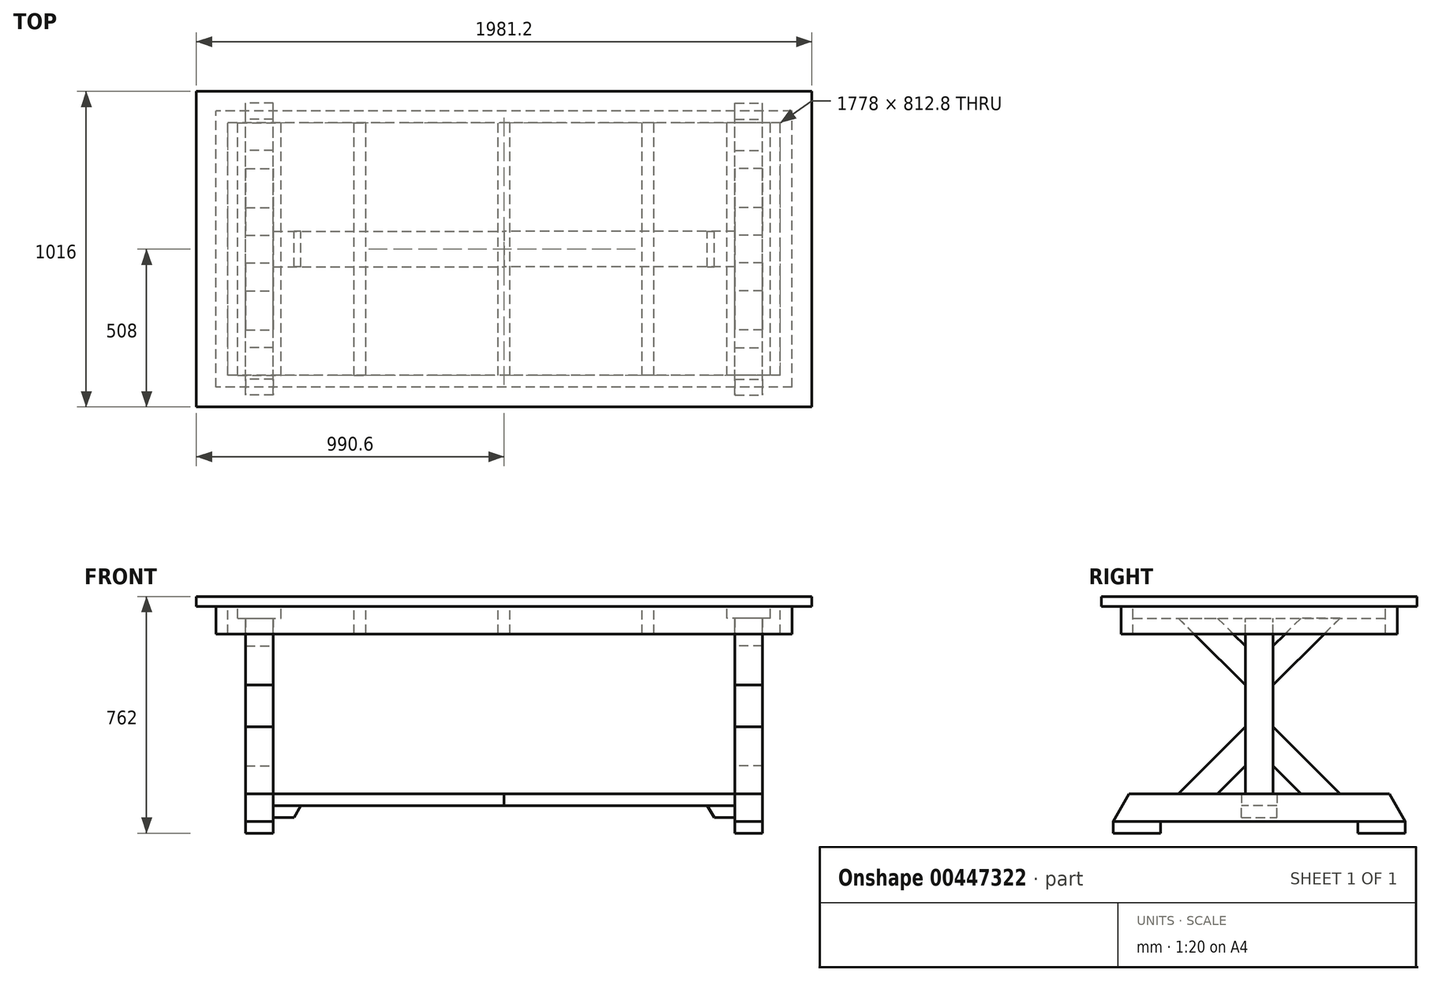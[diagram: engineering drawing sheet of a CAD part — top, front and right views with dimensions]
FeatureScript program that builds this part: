
annotation { "Feature Type Name" : "Feature", "Feature Type Description" : "" }
export const myFeature = defineFeature(function(context is Context, id is Id, definition is map)
    precondition{}
    {
        {
            var Q0;
            Q0=qCreatedBy(makeId("Top.planeOp"),FACE);
            var sketch = newSketch(context, id + "F0", { "sketchPlane" : qUnion([Q0])});
            skLineSegment(sketch, "E0.bottom", {"start": v(990.6, 508) * mm, "end": v(-990.6, 508) * mm});
            skLineSegment(sketch, "E0.top", {"start": v(990.6, -508) * mm, "end": v(-990.6, -508) * mm});
            skLineSegment(sketch, "E0.left", {"start": v(990.6, 508) * mm, "end": v(990.6, -508) * mm});
            skLineSegment(sketch, "E0.right", {"start": v(-990.6, 508) * mm, "end": v(-990.6, -508) * mm});
            skPoint(sketch, "E0.middle", {"position": v(0, 0) * mm});
            skSolve(sketch);
        }
        {
            var Q0;
            Q0 = qSketchRegion(id + "F0", true);
            extrude(context, id + "F1", {"entities" : qUnion([Q0]), "depth" : 31.75 * mm});
        }
        {
            var Q0;
            Q0=makeQuery(id+"F1.opExtrude","CAP_FACE",FACE,{"disambiguationData":[OSD([sQuery(id+"F0.wireOp",EDGE,"E0.bottom"),sQuery(id+"F0.wireOp",EDGE,"E0.top"),sQuery(id+"F0.wireOp",EDGE,"E0.left"),sQuery(id+"F0.wireOp",EDGE,"E0.right")])],"isStart":true});
            var sketch = newSketch(context, id + "F2", { "sketchPlane" : qUnion([Q0])});
            skLineSegment(sketch, "E1.bottom", {"start": v(889, 406.4) * mm, "end": v(-889, 406.4) * mm});
            skLineSegment(sketch, "E1.top", {"start": v(889, -406.4) * mm, "end": v(-889, -406.4) * mm});
            skLineSegment(sketch, "E1.left", {"start": v(889, 406.4) * mm, "end": v(889, -406.4) * mm});
            skLineSegment(sketch, "E1.right", {"start": v(-889, 406.4) * mm, "end": v(-889, -406.4) * mm});
            skPoint(sketch, "E1.middle", {"position": v(0, 0) * mm});
            skLineSegment(sketch, "E2.0", {"start": v(927.1, 444.5) * mm, "end": v(-927.1, 444.5) * mm});
            skLineSegment(sketch, "E2.1", {"start": v(927.1, 444.5) * mm, "end": v(927.1, -444.5) * mm});
            skLineSegment(sketch, "E2.2", {"start": v(927.1, -444.5) * mm, "end": v(-927.1, -444.5) * mm});
            skLineSegment(sketch, "E2.3", {"start": v(-927.1, 444.5) * mm, "end": v(-927.1, -444.5) * mm});
            skLineSegment(sketch, "E3", {"start": v(0, 508) * mm, "end": v(0, 444.5) * mm, "construction": true});
            skLineSegment(sketch, "E4", {"start": v(-927.1, 0) * mm, "end": v(-990.6, 0) * mm, "construction": true});
            skSolve(sketch);
        }
        {
            var Q0;
            Q0 = qSketchRegion(id + "F2", true);
            extrude(context, id + "F3", {"entities" : qUnion([Q0]), "depth" : 88.9 * mm});
        }
        {
            var Q0;
            Q0=makeQuery(id+"F1.opExtrude","CAP_FACE",FACE,{"disambiguationData":[OSD([sQuery(id+"F0.wireOp",EDGE,"E0.bottom"),sQuery(id+"F0.wireOp",EDGE,"E0.top"),sQuery(id+"F0.wireOp",EDGE,"E0.left"),sQuery(id+"F0.wireOp",EDGE,"E0.right")])],"isStart":true});
            var sketch = newSketch(context, id + "F4", { "sketchPlane" : qUnion([Q0])});
            skLineSegment(sketch, "E5.bottom", {"start": v(-857.25, 406.4) * mm, "end": v(-717.55, 406.4) * mm});
            skLineSegment(sketch, "E5.top", {"start": v(-857.25, -406.4) * mm, "end": v(-717.55, -406.4) * mm});
            skLineSegment(sketch, "E5.left", {"start": v(-857.25, 406.4) * mm, "end": v(-857.25, -406.4) * mm});
            skLineSegment(sketch, "E5.right", {"start": v(-717.55, 406.4) * mm, "end": v(-717.55, -406.4) * mm});
            skLineSegment(sketch, "E6", {"start": v(-787.4, 406.4) * mm, "end": v(-787.4, -406.4) * mm, "construction": true});
            skLineSegment(sketch, "E7", {"start": v(0, 0) * mm, "end": v(0, 564.1) * mm, "construction": true});
            skPoint(sketch, "E7.endSnap0", {"position": v(0, 508) * mm});
            skSolve(sketch);
        }
        {
            var Q0;
            Q0 = qSketchRegion(id + "F4", true);
            extrude(context, id + "F5", {"entities" : qUnion([Q0]), "depth" : 38.1 * mm});
        }
        {
            var Q0;
            Q0=makeQuery(id+"F5.opExtrude","CAP_FACE",FACE,{"disambiguationData":[OSD([sQuery(id+"F4.wireOp",EDGE,"E5.bottom"),sQuery(id+"F4.wireOp",EDGE,"E5.top"),sQuery(id+"F4.wireOp",EDGE,"E5.left"),sQuery(id+"F4.wireOp",EDGE,"E5.right")])],"isStart":false});
            var sketch = newSketch(context, id + "F6", { "sketchPlane" : qUnion([Q0])});
            skLineSegment(sketch, "E8.bottom", {"start": v(-831.85, 44.45) * mm, "end": v(-742.95, 44.45) * mm});
            skLineSegment(sketch, "E8.top", {"start": v(-831.85, -44.45) * mm, "end": v(-742.95, -44.45) * mm});
            skLineSegment(sketch, "E8.left", {"start": v(-831.85, 44.45) * mm, "end": v(-831.85, -44.45) * mm});
            skLineSegment(sketch, "E8.right", {"start": v(-742.95, 44.45) * mm, "end": v(-742.95, -44.45) * mm});
            skPoint(sketch, "E9.orphan", {"position": v(-717.55, -44.45) * mm});
            skLineSegment(sketch, "E10", {"start": v(-787.4, 44.45) * mm, "end": v(-787.4, 0) * mm, "construction": true});
            skLineSegment(sketch, "E11", {"start": v(-787.4, 0) * mm, "end": v(-717.55, 0) * mm, "construction": true});
            skSolve(sketch);
        }
        {
            var Q0;
            Q0 = qSketchRegion(id + "F6", true);
            extrude(context, id + "F7", {"entities" : qUnion([Q0]), "depth" : 565.15 * mm});
        }
        {
            var Q0;
            Q0=makeQuery(id+"F7.opExtrude","SWEPT_FACE",FACE,{"disambiguationData":[OSD([sQuery(id+"F6.wireOp",EDGE,"E8.right")])]});
            var sketch = newSketch(context, id + "F8", { "sketchPlane" : qUnion([Q0])});
            skLineSegment(sketch, "E12", {"start": v(-134.25, -38.1) * mm, "end": v(-44.45, -127.9) * mm});
            skLineSegment(sketch, "E13", {"start": v(-44.45, -127.9) * mm, "end": v(-44.45, -320.68) * mm});
            skLineSegment(sketch, "E14", {"start": v(-44.45, -253.63) * mm, "end": v(-259.98, -38.1) * mm});
            skLineSegment(sketch, "E15", {"start": v(-259.98, -38.1) * mm, "end": v(-134.25, -38.1) * mm});
            skLineSegment(sketch, "E16", {"start": v(0, 0) * mm, "end": v(0, -702.78) * mm, "construction": true});
            skLineSegment(sketch, "E17.MirrorCS", {"start": v(134.25, -38.1) * mm, "end": v(44.45, -127.9) * mm});
            skLineSegment(sketch, "E18.MirrorCS", {"start": v(44.45, -127.9) * mm, "end": v(44.45, -320.68) * mm});
            skLineSegment(sketch, "E19.MirrorCS", {"start": v(44.45, -253.63) * mm, "end": v(259.98, -38.1) * mm});
            skLineSegment(sketch, "E20.MirrorCS", {"start": v(259.98, -38.1) * mm, "end": v(134.25, -38.1) * mm});
            skLineSegment(sketch, "E21", {"start": v(44.45, -320.68) * mm, "end": v(-44.45, -320.68) * mm, "construction": true});
            skLineSegment(sketch, "E22.MirrorCS", {"start": v(44.45, -513.45) * mm, "end": v(44.45, -320.68) * mm});
            skLineSegment(sketch, "E23.MirrorCS", {"start": v(134.25, -603.25) * mm, "end": v(44.45, -513.45) * mm});
            skLineSegment(sketch, "E24.MirrorCS", {"start": v(44.45, -387.72) * mm, "end": v(259.98, -603.25) * mm});
            skLineSegment(sketch, "E25.MirrorCS", {"start": v(259.98, -603.25) * mm, "end": v(134.25, -603.25) * mm});
            skLineSegment(sketch, "E26.MirrorCS", {"start": v(-134.25, -603.25) * mm, "end": v(-44.45, -513.45) * mm});
            skLineSegment(sketch, "E27.MirrorCS", {"start": v(-259.98, -603.25) * mm, "end": v(-134.25, -603.25) * mm});
            skLineSegment(sketch, "E28.MirrorCS", {"start": v(-44.45, -387.72) * mm, "end": v(-259.98, -603.25) * mm});
            skLineSegment(sketch, "E29.MirrorCS", {"start": v(-44.45, -513.45) * mm, "end": v(-44.45, -320.68) * mm});
            skSolve(sketch);
        }
        {
            var Q0;
            Q0 = qSketchRegion(id + "F8", true);
            extrude(context, id + "F9", {"entities" : qUnion([Q0]), "oppositeDirection" : true, "depth" : 88.9 * mm});
        }
        {
            var Q0;
            Q0=makeQuery(id+"F7.opExtrude","SWEPT_FACE",FACE,{"disambiguationData":[OSD([sQuery(id+"F6.wireOp",EDGE,"E8.left")])]});
            var sketch = newSketch(context, id + "F10", { "sketchPlane" : qUnion([Q0])});
            skLineSegment(sketch, "E30.bottom", {"start": v(418.57, -603.25) * mm, "end": v(-418.57, -603.25) * mm});
            skLineSegment(sketch, "E30.top", {"start": v(469.9, -692.15) * mm, "end": v(-469.9, -692.15) * mm});
            skPoint(sketch, "E30.middle", {"position": v(0, -647.7) * mm});
            skLineSegment(sketch, "E31", {"start": v(0, 0) * mm, "end": v(0, -647.7) * mm, "construction": true});
            skLineSegment(sketch, "E32", {"start": v(-418.57, -603.25) * mm, "end": v(-469.9, -692.15) * mm});
            skLineSegment(sketch, "E33.MirrorCS", {"start": v(418.57, -603.25) * mm, "end": v(469.9, -692.15) * mm});
            skSolve(sketch);
        }
        {
            var Q0;
            Q0 = qSketchRegion(id + "F10", true);
            extrude(context, id + "F11", {"entities" : qUnion([Q0]), "oppositeDirection" : true, "depth" : 88.9 * mm});
        }
        {
            var Q0;
            Q0=makeQuery(id+"F11.opExtrude","CAP_FACE",FACE,{"disambiguationData":[OSD([sQuery(id+"F10.wireOp",EDGE,"E30.bottom"),sQuery(id+"F10.wireOp",EDGE,"E30.top"),sQuery(id+"F10.wireOp",EDGE,"E30.left"),sQuery(id+"F10.wireOp",EDGE,"E30.right")])],"isStart":true});
            var sketch = newSketch(context, id + "F12", { "sketchPlane" : qUnion([Q0])});
            skLineSegment(sketch, "E34.bottom", {"start": v(-469.9, -692.15) * mm, "end": v(-317.5, -692.15) * mm});
            skLineSegment(sketch, "E34.top", {"start": v(-469.9, -730.25) * mm, "end": v(-317.5, -730.25) * mm});
            skLineSegment(sketch, "E34.left", {"start": v(-469.9, -692.15) * mm, "end": v(-469.9, -730.25) * mm});
            skLineSegment(sketch, "E34.right", {"start": v(-317.5, -692.15) * mm, "end": v(-317.5, -730.25) * mm});
            skPoint(sketch, "E34.middle", {"position": v(-393.7, -711.2) * mm});
            skLineSegment(sketch, "E35", {"start": v(0, -603.25) * mm, "end": v(0, -803.94) * mm, "construction": true});
            skPoint(sketch, "E35.endSnap0", {"position": v(0, -603.25) * mm});
            skLineSegment(sketch, "E36.MirrorCS", {"start": v(469.9, -692.15) * mm, "end": v(317.5, -692.15) * mm});
            skLineSegment(sketch, "E37.MirrorCS", {"start": v(317.5, -692.15) * mm, "end": v(317.5, -730.25) * mm});
            skLineSegment(sketch, "E38.MirrorCS", {"start": v(469.9, -730.25) * mm, "end": v(317.5, -730.25) * mm});
            skLineSegment(sketch, "E39.MirrorCS", {"start": v(469.9, -692.15) * mm, "end": v(469.9, -730.25) * mm});
            skSolve(sketch);
        }
        {
            var Q0;
            Q0 = qSketchRegion(id + "F12", true);
            extrude(context, id + "F13", {"entities" : qUnion([Q0]), "oppositeDirection" : true, "depth" : 88.9 * mm});
        }
        {
            var Q0;
            Q0=qCreatedBy(makeId("Right.planeOp"),FACE);
            var sketch = newSketch(context, id + "F14", { "sketchPlane" : qUnion([Q0])});
            skLineSegment(sketch, "E40.bottom", {"start": v(57.15, -603.25) * mm, "end": v(-57.15, -603.25) * mm});
            skLineSegment(sketch, "E40.top", {"start": v(57.15, -641.35) * mm, "end": v(-57.15, -641.35) * mm});
            skLineSegment(sketch, "E40.left", {"start": v(57.15, -603.25) * mm, "end": v(57.15, -641.35) * mm});
            skLineSegment(sketch, "E40.right", {"start": v(-57.15, -603.25) * mm, "end": v(-57.15, -641.35) * mm});
            skPoint(sketch, "E40.middle", {"position": v(0, -622.3) * mm});
            skLineSegment(sketch, "E41", {"start": v(0, 0) * mm, "end": v(0, -622.3) * mm, "construction": true});
            skSolve(sketch);
        }
        {
            var Q0;
            Q0 = qSketchRegion(id + "F14", true);
            extrude(context, id + "F15", {"entities" : qUnion([Q0]), "endBound" : BoundingType.UP_TO_NEXT, "oppositeDirection" : true, "depth" : 1447.8 * mm});
        }
        {
            var Q0;
            Q0=qCreatedBy(makeId("Front.planeOp"),FACE);
            var sketch = newSketch(context, id + "F16", { "sketchPlane" : qUnion([Q0])});
            skLineSegment(sketch, "E42", {"start": v(0, -88.9) * mm, "end": v(0, -412.82) * mm, "construction": true});
            skLineSegment(sketch, "E43.MirrorCS", {"start": v(-742.95, -641.35) * mm, "end": v(-654.05, -641.35) * mm});
            skLineSegment(sketch, "E44.MirrorCS", {"start": v(-742.95, -679.45) * mm, "end": v(-742.95, -641.35) * mm});
            skLineSegment(sketch, "E45", {"start": v(-742.95, -679.45) * mm, "end": v(-676.05, -679.45) * mm});
            skLineSegment(sketch, "E46", {"start": v(-654.05, -641.35) * mm, "end": v(-676.05, -679.45) * mm});
            skPoint(sketch, "E47.orphan", {"position": v(-654.05, -679.45) * mm});
            skSolve(sketch);
        }
        {
            var Q0;
            Q0 = qSketchRegion(id + "F16", true);
            extrude(context, id + "F17", {"entities" : qUnion([Q0]), "endBound" : BoundingType.SYMMETRIC, "depth" : 114.3 * mm});
        }
        {
            var Q0;
            Q0=makeQuery(id+"F1.opExtrude","CAP_FACE",FACE,{"disambiguationData":[OSD([sQuery(id+"F0.wireOp",EDGE,"E0.bottom"),sQuery(id+"F0.wireOp",EDGE,"E0.top"),sQuery(id+"F0.wireOp",EDGE,"E0.left"),sQuery(id+"F0.wireOp",EDGE,"E0.right")])],"isStart":true});
            var sketch = newSketch(context, id + "F18", { "sketchPlane" : qUnion([Q0])});
            skLineSegment(sketch, "E48.bottom", {"start": v(-482.6, 406.4) * mm, "end": v(-444.5, 406.4) * mm});
            skLineSegment(sketch, "E48.top", {"start": v(-482.6, -406.4) * mm, "end": v(-444.5, -406.4) * mm});
            skLineSegment(sketch, "E48.left", {"start": v(-482.6, 406.4) * mm, "end": v(-482.6, -406.4) * mm});
            skLineSegment(sketch, "E48.right", {"start": v(-444.5, 406.4) * mm, "end": v(-444.5, -406.4) * mm});
            skLineSegment(sketch, "E49", {"start": v(0, 508) * mm, "end": v(0, 0) * mm, "construction": true});
            skPoint(sketch, "E49.endSnap0", {"position": v(0, 508) * mm});
            skLineSegment(sketch, "E50.MirrorCS", {"start": v(482.6, 406.4) * mm, "end": v(444.5, 406.4) * mm});
            skLineSegment(sketch, "E51.MirrorCS", {"start": v(444.5, 406.4) * mm, "end": v(444.5, -406.4) * mm});
            skLineSegment(sketch, "E52.MirrorCS", {"start": v(482.6, 406.4) * mm, "end": v(482.6, -406.4) * mm});
            skLineSegment(sketch, "E53.MirrorCS", {"start": v(482.6, -406.4) * mm, "end": v(444.5, -406.4) * mm});
            skLineSegment(sketch, "E54.bottom", {"start": v(19.05, 406.4) * mm, "end": v(-19.05, 406.4) * mm});
            skLineSegment(sketch, "E54.top", {"start": v(19.05, -406.4) * mm, "end": v(-19.05, -406.4) * mm});
            skLineSegment(sketch, "E54.left", {"start": v(19.05, 406.4) * mm, "end": v(19.05, -406.4) * mm});
            skLineSegment(sketch, "E54.right", {"start": v(-19.05, 406.4) * mm, "end": v(-19.05, -406.4) * mm});
            skPoint(sketch, "E54.middle", {"position": v(0, 0) * mm});
            skSolve(sketch);
        }
        {
            var Q0;
            Q0 = qSketchRegion(id + "F18", true);
            var Q1;
            Q1=makeQuery(id+"F3.opExtrude","CAP_FACE",FACE,{"disambiguationData":[OSD([sQuery(id+"F2.wireOp",EDGE,"E1.bottom"),sQuery(id+"F2.wireOp",EDGE,"E1.top"),sQuery(id+"F2.wireOp",EDGE,"E1.left"),sQuery(id+"F2.wireOp",EDGE,"E1.right"),sQuery(id+"F2.wireOp",EDGE,"E2.0"),sQuery(id+"F2.wireOp",EDGE,"E2.1"),sQuery(id+"F2.wireOp",EDGE,"E2.2"),sQuery(id+"F2.wireOp",EDGE,"E2.3")])],"isStart":false});
            extrude(context, id + "F19", {"entities" : qUnion([Q0]), "endBound" : BoundingType.UP_TO_SURFACE, "endBoundEntityFace" : qUnion([Q1]), "depth" : 25.4 * mm});
        }
        {
            var Q0;
            Q0=makeQuery(id+"F17.opExtrude","SWEPT_BODY",BODY,{"disambiguationData":[OSD([sQuery(id+"F16.wireOp",EDGE,"E43.MirrorCS"),sQuery(id+"F16.wireOp",EDGE,"E44.MirrorCS"),sQuery(id+"F16.wireOp",EDGE,"0bcfbdd2-a0dd-4716-a87c-33451f2bd7550.MirrorCS")])]});
            var Q1;
            Q1=makeQuery(id+"F5.opExtrude","SWEPT_BODY",BODY,{"disambiguationData":[OSD([sQuery(id+"F4.wireOp",EDGE,"E5.bottom"),sQuery(id+"F4.wireOp",EDGE,"E5.top"),sQuery(id+"F4.wireOp",EDGE,"E5.left"),sQuery(id+"F4.wireOp",EDGE,"E5.right")])]});
            var Q2;
            Q2=makeQuery(id+"F7.opExtrude","SWEPT_BODY",BODY,{"disambiguationData":[OSD([sQuery(id+"F6.wireOp",EDGE,"E8.bottom"),sQuery(id+"F6.wireOp",EDGE,"E8.top"),sQuery(id+"F6.wireOp",EDGE,"E8.left"),sQuery(id+"F6.wireOp",EDGE,"E8.right")])]});
            var Q3;
            Q3=makeQuery(id+"F9.opExtrude","SWEPT_BODY",BODY,{"disambiguationData":[OSD([sQuery(id+"F8.wireOp",EDGE,"E12"),sQuery(id+"F8.wireOp",EDGE,"E13"),sQuery(id+"F8.wireOp",EDGE,"E14"),sQuery(id+"F8.wireOp",EDGE,"E15")])]});
            var Q4;
            Q4=makeQuery(id+"F9.opExtrude","SWEPT_BODY",BODY,{"disambiguationData":[OSD([sQuery(id+"F8.wireOp",EDGE,"E17.MirrorCS"),sQuery(id+"F8.wireOp",EDGE,"E18.MirrorCS"),sQuery(id+"F8.wireOp",EDGE,"E19.MirrorCS"),sQuery(id+"F8.wireOp",EDGE,"E20.MirrorCS")])]});
            var Q5;
            Q5=makeQuery(id+"F9.opExtrude","SWEPT_BODY",BODY,{"disambiguationData":[OSD([sQuery(id+"F8.wireOp",EDGE,"E22.MirrorCS"),sQuery(id+"F8.wireOp",EDGE,"E23.MirrorCS"),sQuery(id+"F8.wireOp",EDGE,"E24.MirrorCS"),sQuery(id+"F8.wireOp",EDGE,"E25.MirrorCS")])]});
            var Q6;
            Q6=makeQuery(id+"F9.opExtrude","SWEPT_BODY",BODY,{"disambiguationData":[OSD([sQuery(id+"F8.wireOp",EDGE,"E26.MirrorCS"),sQuery(id+"F8.wireOp",EDGE,"E27.MirrorCS"),sQuery(id+"F8.wireOp",EDGE,"E28.MirrorCS"),sQuery(id+"F8.wireOp",EDGE,"E29.MirrorCS")])]});
            var Q7;
            Q7=makeQuery(id+"F11.opExtrude","SWEPT_BODY",BODY,{"disambiguationData":[OSD([sQuery(id+"F10.wireOp",EDGE,"E30.bottom"),sQuery(id+"F10.wireOp",EDGE,"E30.top"),sQuery(id+"F10.wireOp",EDGE,"E30.left"),sQuery(id+"F10.wireOp",EDGE,"E30.right")])]});
            var Q8;
            Q8=makeQuery(id+"F13.opExtrude","SWEPT_BODY",BODY,{"disambiguationData":[OSD([sQuery(id+"F12.wireOp",EDGE,"E34.bottom"),sQuery(id+"F12.wireOp",EDGE,"E34.top"),sQuery(id+"F12.wireOp",EDGE,"E34.left"),sQuery(id+"F12.wireOp",EDGE,"E34.right")])]});
            var Q9;
            Q9=makeQuery(id+"F13.opExtrude","SWEPT_BODY",BODY,{"disambiguationData":[OSD([sQuery(id+"F12.wireOp",EDGE,"E36.MirrorCS"),sQuery(id+"F12.wireOp",EDGE,"E37.MirrorCS"),sQuery(id+"F12.wireOp",EDGE,"E38.MirrorCS"),sQuery(id+"F12.wireOp",EDGE,"E39.MirrorCS")])]});
            var Q10;
            Q10=makeQuery(id+"F15.opExtrude","SWEPT_BODY",BODY,{"disambiguationData":[OSD([sQuery(id+"F14.wireOp",EDGE,"E40.bottom"),sQuery(id+"F14.wireOp",EDGE,"E40.top"),sQuery(id+"F14.wireOp",EDGE,"E40.left"),sQuery(id+"F14.wireOp",EDGE,"E40.right")])]});
            var Q11;
            Q11=qCreatedBy(makeId("Right.planeOp"),FACE);
            mirror(context, id + "F20", {"entities" : qUnion([Q0, Q1, Q2, Q3, Q4, Q5, Q6, Q7, Q8, Q9, Q10]), "mirrorPlane" : qUnion([Q11])});
        }
    });
